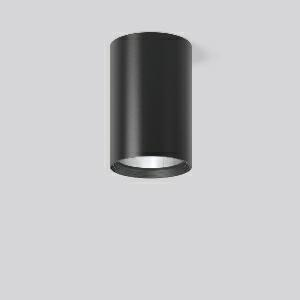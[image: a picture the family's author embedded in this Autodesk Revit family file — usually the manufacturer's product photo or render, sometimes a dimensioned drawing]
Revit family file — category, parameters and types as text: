
# Revit family: heledon_maxi_a_931216_003_879c
name_source: partatom
category: Lighting Fixtures
units: mm (PartAtom-declared; Revit-internal decimal feet)

## family parameters
Cut with Voids When Loaded = No
Host = Face
Light Source = No
Part Type = Normal
Room Calculation Point = No
Round Connector Dimension = Use Diameter
Shared = No

## types (1)
- HELEDON maxi A (1 x LED Modul 930, 3250 lm, 3000)
    Apparent Load = 25 VA
    Approval mark = CE
    CIE Flux Codes = 100 100 100 100 100
    Color Rendering = 90
    Color Temperature = 3000
    Default Elevation = 1800 mm
    Description = Series: HELEDON maxi
Cylindrical surface-mounted downlight. Housing: die-cast aluminium, powder-coated. Internal ceiling frame polycarbonate with bayonet mounting. Black plastic ring and recessed LED to prevent glare from the side. Optical assembly with reflector made of MIRO-Silver with 98% total light reflection for outstanding efficiency - can be changed without tools. Best colour rendering index Ra>90. Suitable for Ceiling mounting. Easy installation with a separate ceiling frame with bayonet mounting and plug connection. Driver integrated. Connected via plug-in connector. High quality converter without flickering and stroboscopic effect. The following accessories can be mounted without use of tools: interchangeable lenses, decorative glasses, honeycomb louvre, clear and frosted diffusers, white interchangeable plastic ring. 
Colour: deep black, matt (RAL 9005)
Diameter: 123 mm
Height: 183 mm
Lamp: LED
Socket: without socket
Colour temperature: 3000K
Colour rendering index (CRI): 92
System power: 25 W
Rated luminous flux: 3250 lm
Luminous efficiency: 130 lm/W
Control gear: Regulated power supply
Protection class: I
Type of protection: IP 20
    Height = 183 mm
    Lamp = 1 x LED Modul 930
    Lamp Light Flux = 3250 lm
    Lamp count = 1
    Length = 123 mm
    Lifetime = 50000 h
    Luminous efficacy = 130 lm/W
    Manufacturer = RZB
    ModVariant = No
    Model = 931216.003
    Mounting Place = Ceiling
    Mounting Type = Surface mounted
    Number of Poles = 1
    OnlyDefault = Yes
    Power Factor = 1
    Product Name = HELEDON maxi A
    Product group = Surface mounted downlights
    ProductGroupID = 302
    Protection Class = Protection class I
    Protection Degree = IP 20
    RLX_Detail_Level = 1
    RLX_Emergency_Light_Flux = 0 lm
    RLX_Emergency_Type = 0
    RLX_Emergency_Type_DB = No
    RlxData = <blob elided: 98221 chars, md5=e8889179>
    Socket = socket
    Standby Power = 0 W
    System Light Flux = 3250 lm
    System Power = 25 W
    Type Comments = Product without accessories
    Type Image = 931192.003.jpg
    URL = http://relux.com
    VarID = ---
    Voltage = 230 V
    Voltage Range = 220-240 V
    Weight = 0.00 kg
    Width = 0 mm  [stored 0 ft]

note: [stored X ft] marks values corroborated as IEEE doubles in the binary element streams (Revit-internal decimal feet)

## geometry (parser evidence)
native form markers: Blend x4, Sweep x10
no freeform markers — native parametric forms only
